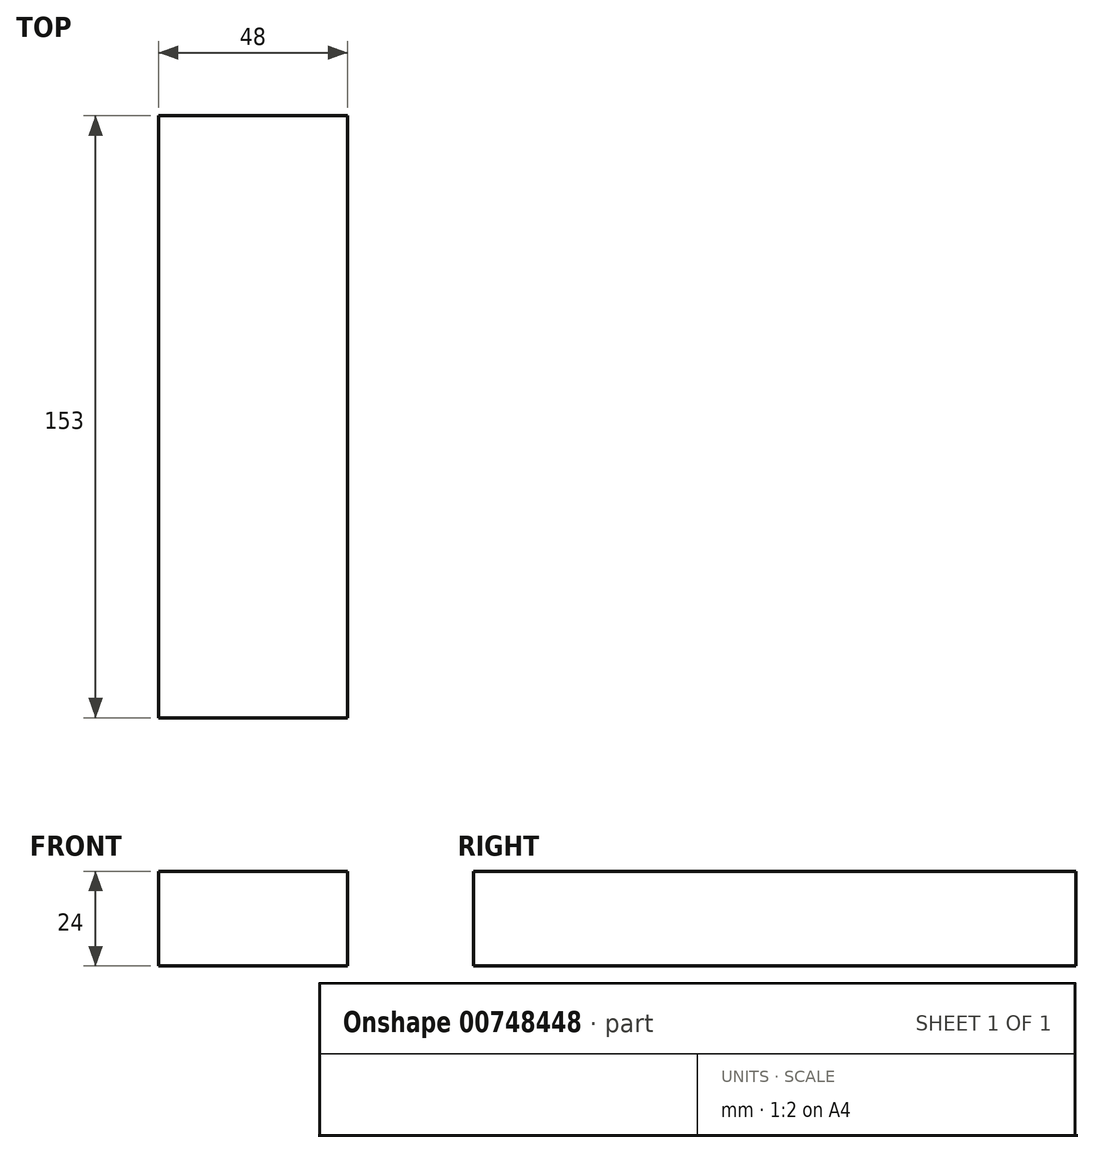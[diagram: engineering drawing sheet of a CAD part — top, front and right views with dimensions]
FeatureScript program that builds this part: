
annotation { "Feature Type Name" : "Feature", "Feature Type Description" : "" }
export const myFeature = defineFeature(function(context is Context, id is Id, definition is map)
    precondition{}
    {
        {
            var Q0;
            Q0=qCreatedBy(makeId("Front.planeOp"),FACE);
            var sketch = newSketch(context, id + "F0", { "sketchPlane" : qUnion([Q0])});
            skLineSegment(sketch, "E0.bottom", {"start": v(0, 0) * mm, "end": v(48, 0) * mm});
            skLineSegment(sketch, "E0.top", {"start": v(0, 24) * mm, "end": v(48, 24) * mm});
            skLineSegment(sketch, "E0.left", {"start": v(0, 0) * mm, "end": v(0, 24) * mm});
            skLineSegment(sketch, "E0.right", {"start": v(48, 0) * mm, "end": v(48, 24) * mm});
            skSolve(sketch);
        }
        {
            var Q0;
            Q0=makeQuery(id+"F0.imprint","IMPRINT",FACE,{"disambiguationData":[TD([[makeQuery(id+"F0.imprint","IMPRINT",EDGE,{"derivedFrom":sQuery(id+"F0.wireOp",EDGE,"E0.bottom")}),1.0]])]});
            extrude(context, id + "F1", {"entities" : qUnion([Q0]), "depth" : 153 * mm, "offsetDistance" : 25 * mm});
        }
    });
